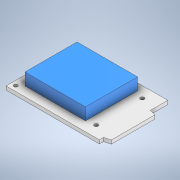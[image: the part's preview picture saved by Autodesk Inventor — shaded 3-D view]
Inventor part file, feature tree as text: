
AUTODESK INVENTOR PART (.ipt)
format: ipt  version: 2022 (Build 260153000, 153)  size: 168,960 bytes
history: native  units: in
note: dims shown in document units (in); Inventor stores cm internally (conversion verified against a paired STEP export)
features: sketch x5, extrude x3
ambient origin geometry x8: Origin, YZ Plane, XZ Plane, XY Plane, X Axis, Y Axis, Z Axis, Center Point
bodies: Solid1 (feature_tree)
feature tree (8):
  extrude  "Extrusion1"  Depth=2.2595in
  extrude  "Extrusion2"  Depth=1.438in
  extrude  "Extrusion3"  Depth=0.202in
  sketch  "Sketch4"  dims[d6=0.12in d7=0.0in]
  sketch  "Sketch5"  dims[d8=0.091in d9=0.1065in d10=0.125in d11=0.122in d12=0.411in d13=0.305in d14=0.305in d15=0.125in d16=0.125in d17=0.125in d18=0.125in d19=0.12in d20=0.0in d21=0.4in d22=0.0in d23=0.9623in d24=0.9623in d25=1.3898in d26=1.3898in d27=1.0683in d28=1.0683in d29=0.7622in d30=0.7622in]
  sketch  "Sketch1"  dims[d0=3.0835in d1=2.2595in]
  sketch  "Sketch2"  dims[d2=1.5505in d3=1.438in]
  sketch  "Sketch3"  dims[d4=0.572in d5=0.202in]
